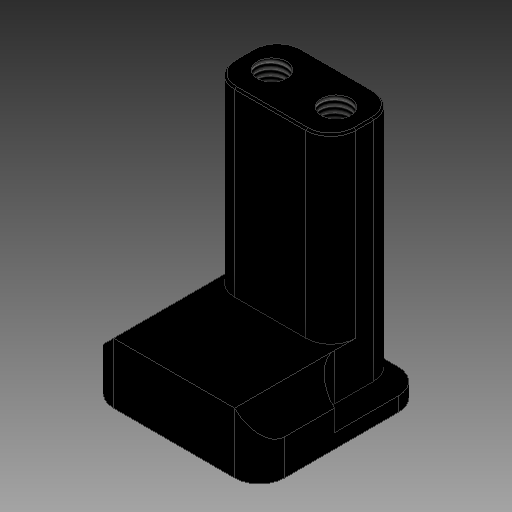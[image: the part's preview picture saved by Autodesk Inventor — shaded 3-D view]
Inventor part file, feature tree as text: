
AUTODESK INVENTOR PART (.ipt)
format: ipt  version: 2019 (Build 230136000, 136)  size: 186,368 bytes
history: native  units: mm
features: extrude x3, other x3, hole x2, chamfer x2, fillet x1
ambient origin geometry x8: Origin, YZ Plane, XZ Plane, XY Plane, X Axis, Y Axis, Z Axis, Center Point
bodies: Solid1 (feature_tree)
feature tree (11):
  extrude  "Base"  Depth=23.0mm
  extrude  "Pillar"  Depth=11.5mm
  extrude  "Base Cutouts"  Depth=24.0mm
  hole  "Holes"  [1 undecoded]
  chamfer  "Base Chamfer"  Distance=8.5mm
  fillet  "Pillar Fillet"  [1 undecoded]
  chamfer  "Pillar Chamfer"  Distance=9.5mm
  other  "Base Outline"
  other  "Pillar Outline"
  other  "Base Cutouts Outline"
  hole  "Hole Positions"  [1 undecoded]
note: 3 required parameter values undecoded (feature->parameter linkage not recoverable at this tier; creation-order binding heuristic only, values carry confidence <= 0.55)
